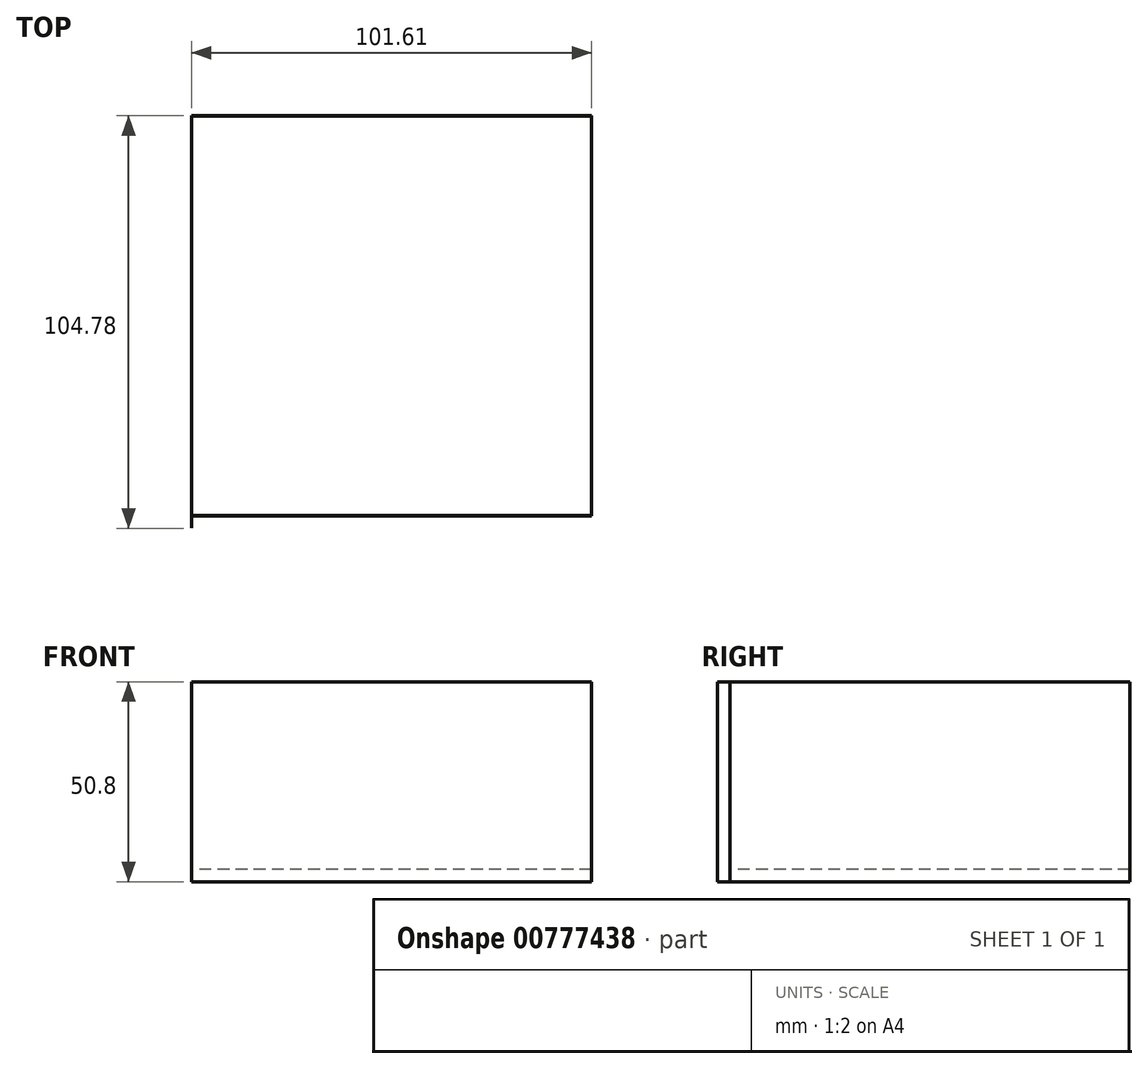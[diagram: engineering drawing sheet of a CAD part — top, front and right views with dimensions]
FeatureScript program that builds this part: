
annotation { "Feature Type Name" : "Feature", "Feature Type Description" : "" }
export const myFeature = defineFeature(function(context is Context, id is Id, definition is map)
    precondition{}
    {
        {
            var Q0;
            Q0=qCreatedBy(makeId("Top.planeOp"),FACE);
            var sketch = newSketch(context, id + "F0", { "sketchPlane" : qUnion([Q0])});
            skLineSegment(sketch, "E0.bottom", {"start": v(-50.8, 50.8) * mm, "end": v(50.8, 50.8) * mm});
            skLineSegment(sketch, "E0.top", {"start": v(-50.8, -50.8) * mm, "end": v(50.8, -50.8) * mm});
            skLineSegment(sketch, "E0.left", {"start": v(-50.8, 50.8) * mm, "end": v(-50.8, -50.8) * mm});
            skLineSegment(sketch, "E0.right", {"start": v(50.8, 50.8) * mm, "end": v(50.8, -50.8) * mm});
            skPoint(sketch, "E0.middle", {"position": v(0, 0) * mm});
            skSolve(sketch);
        }
        {
            var Q0;
            Q0=makeQuery(id+"F0.imprint","IMPRINT",FACE,{"disambiguationData":[TD([[makeQuery(id+"F0.imprint","IMPRINT",EDGE,{"derivedFrom":sQuery(id+"F0.wireOp",EDGE,"E0.bottom")}),-1.0]])]});
            extrude(context, id + "F1", {"entities" : qUnion([Q0]), "depth" : 3.17 * mm, "offsetDistance" : 25.4 * mm});
        }
        {
            var Q0;
            Q0=makeQuery(id+"F1.opExtrude","SWEPT_FACE",FACE,{"disambiguationData":[OSD([sQuery(id+"F0.wireOp",EDGE,"E0.top")])]});
            var sketch = newSketch(context, id + "F2", { "sketchPlane" : qUnion([Q0])});
            skLineSegment(sketch, "E1.bottom", {"start": v(50.8, 0) * mm, "end": v(-50.8, 0) * mm});
            skLineSegment(sketch, "E1.top", {"start": v(50.8, 50.8) * mm, "end": v(-50.8, 50.8) * mm});
            skLineSegment(sketch, "E1.left", {"start": v(50.8, 0) * mm, "end": v(50.8, 50.8) * mm});
            skLineSegment(sketch, "E1.right", {"start": v(-50.8, 0) * mm, "end": v(-50.8, 50.8) * mm});
            skSolve(sketch);
        }
        {
            var Q0;
            Q0 = qSketchRegion(id + "F2", true);
            extrude(context, id + "F3", {"entities" : qUnion([Q0]), "operationType" : NewBodyOperationType.ADD, "depth" : 1 / 203.2 * mm, "offsetDistance" : 25.4 * mm});
        }
        {
            var Q0;
            Q0=makeQuery(id+"F1.opExtrude","SWEPT_FACE",FACE,{"disambiguationData":[OSD([sQuery(id+"F0.wireOp",EDGE,"E0.bottom")])]});
            var sketch = newSketch(context, id + "F4", { "sketchPlane" : qUnion([Q0])});
            skLineSegment(sketch, "E2.bottom", {"start": v(-50.8, 0) * mm, "end": v(50.8, 0) * mm});
            skLineSegment(sketch, "E2.top", {"start": v(-50.8, 50.8) * mm, "end": v(50.8, 50.8) * mm});
            skLineSegment(sketch, "E2.left", {"start": v(-50.8, 0) * mm, "end": v(-50.8, 50.8) * mm});
            skLineSegment(sketch, "E2.right", {"start": v(50.8, 0) * mm, "end": v(50.8, 50.8) * mm});
            skSolve(sketch);
        }
        {
            var Q0;
            {var subQ0=sQuery(id+"F4.wireOp",EDGE,"E2.top");Q0=makeQuery(id+"F4.imprint","IMPRINT",FACE,{"disambiguationData":[TD([[makeQuery(id+"F4.imprint","IMPRINT",EDGE,{"derivedFrom":subQ0}),-1.0]])]});}
            var Q1;
            {var subQ0=sQuery(id+"F4.wireOp",EDGE,"E2.bottom");Q1=makeQuery(id+"F4.imprint","IMPRINT",FACE,{"disambiguationData":[TD([[makeQuery(id+"F4.imprint","IMPRINT",EDGE,{"derivedFrom":subQ0}),-1.0]])]});}
            extrude(context, id + "F5", {"entities" : qUnion([Q0, Q1]), "operationType" : NewBodyOperationType.ADD, "oppositeDirection" : true, "depth" : 1 / 203.2 * mm, "offsetDistance" : 25.4 * mm});
        }
        {
            var Q0;
            Q0=makeQuery(id+"F3.boolean.opBoolean","MERGE",FACE,{"derivedFrom":[makeQuery(id+"F1.opExtrude","SWEPT_FACE",FACE,{"disambiguationData":[OSD([sQuery(id+"F0.wireOp",EDGE,"E0.right")])]}),makeQuery(id+"F3.opExtrude","SWEPT_FACE",FACE,{"disambiguationData":[OSD([sQuery(id+"F2.wireOp",EDGE,"E1.left")])]})]});
            var sketch = newSketch(context, id + "F6", { "sketchPlane" : qUnion([Q0])});
            skLineSegment(sketch, "E3.bottom", {"start": v(50.8, 0) * mm, "end": v(-53.98, 0) * mm});
            skLineSegment(sketch, "E3.top", {"start": v(50.8, 50.8) * mm, "end": v(-53.98, 50.8) * mm});
            skLineSegment(sketch, "E3.left", {"start": v(50.8, 0) * mm, "end": v(50.8, 50.8) * mm});
            skLineSegment(sketch, "E3.right", {"start": v(-53.98, 0) * mm, "end": v(-53.98, 50.8) * mm});
            skSolve(sketch);
        }
        {
            var Q0;
            Q0=makeQuery(id+"F3.boolean.opBoolean","MERGE",FACE,{"derivedFrom":[makeQuery(id+"F1.opExtrude","SWEPT_FACE",FACE,{"disambiguationData":[OSD([sQuery(id+"F0.wireOp",EDGE,"E0.left")])]}),makeQuery(id+"F3.opExtrude","SWEPT_FACE",FACE,{"disambiguationData":[OSD([sQuery(id+"F2.wireOp",EDGE,"E1.right")])]})]});
            var Q1;
            {var subQ4=makeQuery(id+"F1.opExtrude","CAP_EDGE",EDGE,{"disambiguationData":[OSD([sQuery(id+"F0.wireOp",EDGE,"E0.right")])],"isStart":false});Q1=makeQuery(id+"F6.imprint","IMPRINT",FACE,{"disambiguationData":[TD([[makeQuery(id+"F6.imprint","IMPRINT",EDGE,{"derivedFrom":subQ4}),-1.0]])]});}
            extrude(context, id + "F7", {"entities" : qUnion([Q0, Q1]), "operationType" : NewBodyOperationType.ADD, "depth" : 1 / 203.2 * mm, "offsetDistance" : 25.4 * mm});
        }
        {
            var Q0;
            Q0=makeQuery(id+"F7.opExtrude","CAP_FACE",FACE,{"disambiguationData":[OSD([sQuery(id+"F0.wireOp",EDGE,"E0.left"),sQuery(id+"F2.wireOp",EDGE,"E1.right")])],"isStart":false});
            var sketch = newSketch(context, id + "F8", { "sketchPlane" : qUnion([Q0])});
            skLineSegment(sketch, "E4.bottom", {"start": v(-50.8, 0) * mm, "end": v(53.98, 0) * mm});
            skLineSegment(sketch, "E4.top", {"start": v(-50.8, 50.8) * mm, "end": v(53.98, 50.8) * mm});
            skLineSegment(sketch, "E4.left", {"start": v(-50.8, 0) * mm, "end": v(-50.8, 50.8) * mm});
            skLineSegment(sketch, "E4.right", {"start": v(53.98, 0) * mm, "end": v(53.98, 50.8) * mm});
            skSolve(sketch);
        }
        {
            var Q0;
            {var subQ1=sQuery(id+"F8.wireOp",EDGE,"E4.bottom");Q0=makeQuery(id+"F8.imprint","IMPRINT",FACE,{"disambiguationData":[TD([[makeQuery(id+"F8.imprint","IMPRINT",EDGE,{"derivedFrom":subQ1}),1.0]])]});}
            var Q1;
            {var subQ5=makeQuery(id+"F7.opExtrude","CAP_EDGE",EDGE,{"disambiguationData":[OSD([sQuery(id+"F0.wireOp",EDGE,"E0.left")])],"isStart":false});Q1=makeQuery(id+"F8.imprint","IMPRINT",FACE,{"disambiguationData":[TD([[makeQuery(id+"F8.imprint","IMPRINT",EDGE,{"derivedFrom":subQ5}),1.0]])]});}
            extrude(context, id + "F9", {"entities" : qUnion([Q0, Q1]), "operationType" : NewBodyOperationType.ADD, "depth" : 1 / 203.2 * mm, "offsetDistance" : 25.4 * mm});
        }
    });
